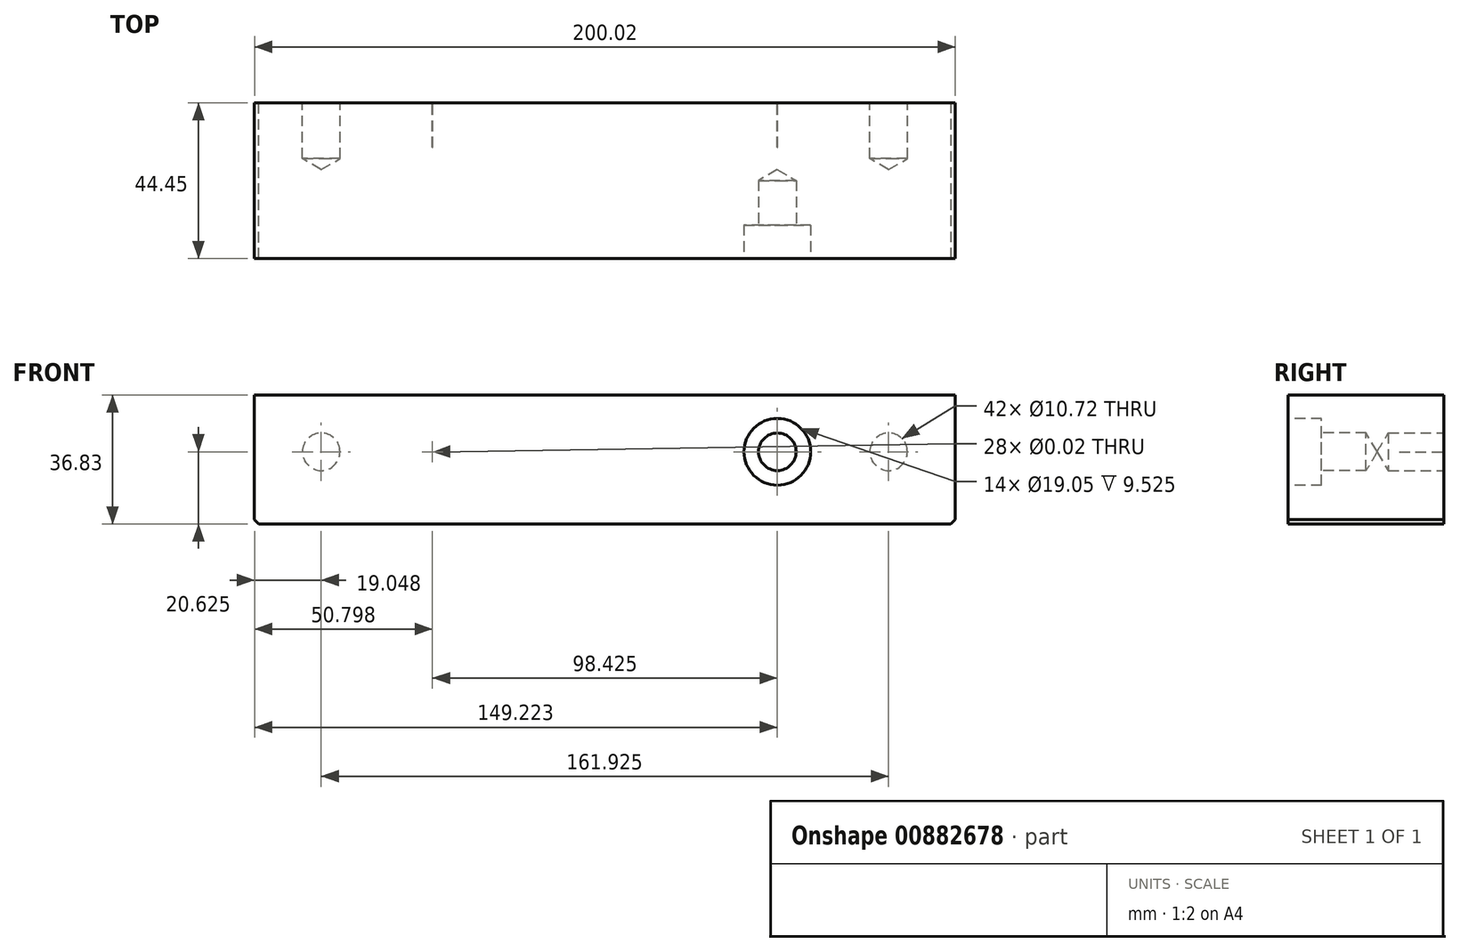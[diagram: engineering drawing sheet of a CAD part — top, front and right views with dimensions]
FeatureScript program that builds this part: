
annotation { "Feature Type Name" : "Feature", "Feature Type Description" : "" }
export const myFeature = defineFeature(function(context is Context, id is Id, definition is map)
    precondition{}
    {
        {
            var Q0;
            Q0=qCreatedBy(makeId("Top.planeOp"),FACE);
            var sketch = newSketch(context, id + "F0", { "sketchPlane" : qUnion([Q0])});
            skLineSegment(sketch, "E0.bottom", {"start": v(-100.2, 38.28) * mm, "end": v(99.82, 38.28) * mm});
            skLineSegment(sketch, "E0.top", {"start": v(-100.2, -37.92) * mm, "end": v(99.82, -37.92) * mm});
            skLineSegment(sketch, "E0.left", {"start": v(-100.2, 38.28) * mm, "end": v(-100.2, -37.92) * mm});
            skLineSegment(sketch, "E0.right", {"start": v(99.82, 38.28) * mm, "end": v(99.82, -37.92) * mm});
            skSolve(sketch);
        }
        {
            var Q0;
            Q0=makeQuery(id+"F0.imprint","IMPRINT",FACE,{"disambiguationData":[TD([[makeQuery(id+"F0.imprint","IMPRINT",EDGE,{"derivedFrom":sQuery(id+"F0.wireOp",EDGE,"E0.bottom")}),-1.0]])]});
            extrude(context, id + "F1", {"entities" : qUnion([Q0]), "depth" : 36.83 * mm, "offsetDistance" : 25.4 * mm});
        }
        {
            var Q0;
            Q0=makeQuery(id+"F1.opExtrude","SWEPT_FACE",FACE,{"disambiguationData":[OSD([sQuery(id+"F0.wireOp",EDGE,"E0.bottom")])]});
            extrude(context, id + "F2", {"entities" : qUnion([Q0]), "operationType" : NewBodyOperationType.REMOVE, "oppositeDirection" : true, "depth" : 31.75 * mm, "offsetDistance" : 25.4 * mm});
        }
        {
            var Q0;
            Q0=makeQuery(id+"F2.boolean.opBoolean","COPY",FACE,{"derivedFrom":makeQuery(id+"F2.opExtrude","CAP_FACE",FACE,{"disambiguationData":[OSD([sQuery(id+"F0.wireOp",EDGE,"E0.bottom")])],"isStart":false})});
            var sketch = newSketch(context, id + "F3", { "sketchPlane" : qUnion([Q0])});
            skLineSegment(sketch, "E1.bottom", {"start": v(-99.82, 0) * mm, "end": v(-80.77, 0) * mm});
            skLineSegment(sketch, "E1.top", {"start": v(-99.82, 20.62) * mm, "end": v(-80.77, 20.62) * mm, "construction": true});
            skLineSegment(sketch, "E1.left", {"start": v(-99.82, 0) * mm, "end": v(-99.82, 20.62) * mm});
            skLineSegment(sketch, "E1.right", {"start": v(-80.77, 0) * mm, "end": v(-80.77, 20.62) * mm, "construction": true});
            skLineSegment(sketch, "E2", {"start": v(-80.77, 20.62) * mm, "end": v(-49.02, 20.62) * mm, "construction": true});
            skCircle(sketch, "E3", {"center": v(-49.02, 20.62) * mm, "radius": 5.93 * mm});
            skCircle(sketch, "E4", {"center": v(-80.77, 20.62) * mm, "radius": 5.4 * mm});
            skLineSegment(sketch, "E5", {"start": v(0.19, 36.83) * mm, "end": v(0.19, 0) * mm});
            skCircle(sketch, "E6.MirrorC", {"center": v(49.4, 20.62) * mm, "radius": 5.93 * mm});
            skCircle(sketch, "E7.MirrorC", {"center": v(81.15, 20.62) * mm, "radius": 5.4 * mm});
            skSolve(sketch);
        }
        {
            var Q0;
            Q0=sQuery(id+"F3.wireOp",VERTEX,"6420fb8b-75b4-417c-8158-19be04d08c0f1.MirrorCS.start");
            var Q1;
            Q1=sQuery(id+"F3.wireOp",VERTEX,"E1.top.end");
            var Q2;
            Q2=sQuery(id+"F3.wireOp",VERTEX,"e42a928c-d6da-488d-aa43-b77a77ec39e20.MirrorC.center");
            var Q3;
            Q3=sQuery(id+"F3.wireOp",VERTEX,"E7.MirrorC.center");
            var Q4;
            Q4=makeQuery(id+"F1.opExtrude","SWEPT_BODY",BODY,{"disambiguationData":[OSD([sQuery(id+"F0.wireOp",EDGE,"E0.bottom"),sQuery(id+"F0.wireOp",EDGE,"E0.top"),sQuery(id+"F0.wireOp",EDGE,"E0.left"),sQuery(id+"F0.wireOp",EDGE,"E0.right")])]});
            hole(context, id + "F4", {"style" : HoleStyle.SIMPLE, "endStyle" : HoleEndStyle.BLIND, "standardTappedOrClearance" : lookupTablePath({ "standard" : "ANSI", "engagement" : "75%", "pitch" : "13 tpi", "size" : "1/2", "type" : "Tapped" }), "standardBlindInLast" : lookupTablePath({ "standard" : "ANSI", "engagement" : "75%", "pitch" : "13 tpi", "size" : "1/2", "type" : "Tapped" }), "holeDiameter" : 10.72 * mm, "majorDiameter" : 12.7 * mm, "showTappedDepth" : true, "holeDepth" : 15.88 * mm, "isTappedThrough" : true, "tappedDepth" : 15.88 * mm, "tapClearance" : 0, "locations" : qUnion([Q0, Q1, Q2, Q3]), "scope" : qUnion([Q4])});
        }
        {
            var Q0;
            Q0=sQuery(id+"F3.wireOp",VERTEX,"6420fb8b-75b4-417c-8158-19be04d08c0f1.MirrorCS.end");
            var Q1;
            Q1=sQuery(id+"F3.wireOp",VERTEX,"E2.end");
            var Q2;
            Q2=sQuery(id+"F3.wireOp",VERTEX,"569afc53-8b23-4811-9af9-951c38216e830.MirrorC.center");
            var Q3;
            Q3=sQuery(id+"F3.wireOp",VERTEX,"E6.MirrorC.center");
            var Q4;
            Q4=makeQuery(id+"F1.opExtrude","SWEPT_BODY",BODY,{"disambiguationData":[OSD([sQuery(id+"F0.wireOp",EDGE,"E0.bottom"),sQuery(id+"F0.wireOp",EDGE,"E0.top"),sQuery(id+"F0.wireOp",EDGE,"E0.left"),sQuery(id+"F0.wireOp",EDGE,"E0.right")])]});
            hole(context, id + "F5", {"style" : HoleStyle.SIMPLE, "endStyle" : HoleEndStyle.BLIND, "standardTappedOrClearance" : lookupTablePath({ "standard" : "ANSI", "size" : "1/2 (0.5)", "type" : "Drilled" }), "standardBlindInLast" : lookupTablePath({ "standard" : "ANSI", "size" : "1/2", "type" : "Drilled" }), "holeDiameter" : 1 / 50.8 * mm, "majorDiameter" : 12.7 * mm, "holeDepth" : 12.7 * mm, "isTappedThrough" : true, "tappedDepth" : 15.88 * mm, "tapClearance" : 3, "locations" : qUnion([Q0, Q1, Q2, Q3]), "scope" : qUnion([Q4])});
        }
        {
            var Q0;
            Q0=makeQuery(id+"F1.opExtrude","CAP_EDGE",EDGE,{"disambiguationData":[OSD([sQuery(id+"F0.wireOp",EDGE,"E0.left")])],"isStart":true});
            var Q1;
            Q1=makeQuery(id+"F1.opExtrude","CAP_EDGE",EDGE,{"disambiguationData":[OSD([sQuery(id+"F0.wireOp",EDGE,"E0.right")])],"isStart":true});
            chamfer(context, id + "F6", {"entities" : qUnion([Q0, Q1]), "width" : 1.27 * mm, "tangentPropagation" : true});
        }
        {
            var Q0;
            Q0=makeQuery(id+"F1.opExtrude","SWEPT_FACE",FACE,{"disambiguationData":[OSD([sQuery(id+"F0.wireOp",EDGE,"E0.top")])]});
            var sketch = newSketch(context, id + "F7", { "sketchPlane" : qUnion([Q0])});
            skCircle(sketch, "E8", {"center": v(49.02, 20.62) * mm, "radius": 9.53 * mm});
            skSolve(sketch);
        }
        {
            var Q0;
            Q0=makeQuery(id+"F7.imprint","IMPRINT",FACE,{"disambiguationData":[TD([[makeQuery(id+"F7.imprint","IMPRINT",EDGE,{"derivedFrom":sQuery(id+"F7.wireOp",EDGE,"E8")}),1.0]])]});
            extrude(context, id + "F8", {"entities" : qUnion([Q0]), "operationType" : NewBodyOperationType.REMOVE, "oppositeDirection" : true, "depth" : 9.52 * mm, "offsetDistance" : 25.4 * mm});
        }
        {
            var Q0;
            Q0=makeQuery(id+"F8.boolean.opBoolean","COPY",FACE,{"derivedFrom":makeQuery(id+"F8.opExtrude","CAP_FACE",FACE,{"disambiguationData":[OSD([sQuery(id+"F7.wireOp",EDGE,"E8")])],"isStart":false})});
            var sketch = newSketch(context, id + "F9", { "sketchPlane" : qUnion([Q0])});
            skPoint(sketch, "E9", {"position": v(49.02, 20.62) * mm});
            skSolve(sketch);
        }
        {
            var Q0;
            Q0=sQuery(id+"F9.wireOp",VERTEX,"E9");
            var Q1;
            Q1=makeQuery(id+"F1.opExtrude","SWEPT_BODY",BODY,{"disambiguationData":[OSD([sQuery(id+"F0.wireOp",EDGE,"E0.bottom"),sQuery(id+"F0.wireOp",EDGE,"E0.top"),sQuery(id+"F0.wireOp",EDGE,"E0.left"),sQuery(id+"F0.wireOp",EDGE,"E0.right")])]});
            hole(context, id + "F10", {"style" : HoleStyle.SIMPLE, "endStyle" : HoleEndStyle.BLIND, "standardTappedOrClearance" : lookupTablePath({ "standard" : "ANSI", "engagement" : "75%", "pitch" : "13 tpi", "size" : "1/2", "type" : "Tapped" }), "standardBlindInLast" : lookupTablePath({ "standard" : "ANSI", "engagement" : "75%", "pitch" : "13 tpi", "size" : "1/2", "type" : "Tapped" }), "holeDiameter" : 10.72 * mm, "majorDiameter" : 12.7 * mm, "showTappedDepth" : true, "holeDepth" : 12.7 * mm, "isTappedThrough" : true, "tappedDepth" : 12.7 * mm, "tapClearance" : 0, "locations" : qUnion([Q0]), "scope" : qUnion([Q1])});
        }
    });
